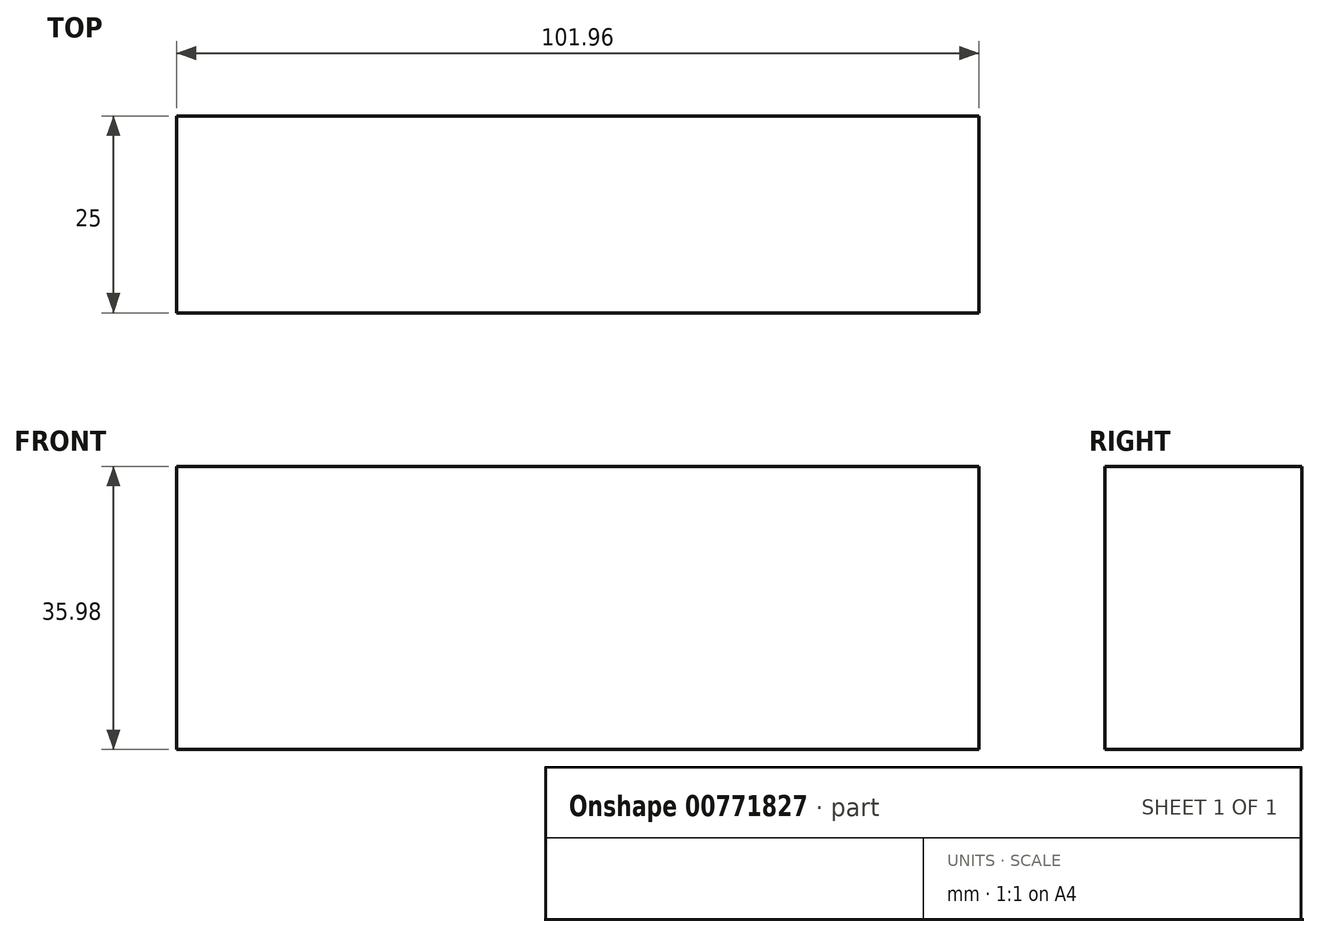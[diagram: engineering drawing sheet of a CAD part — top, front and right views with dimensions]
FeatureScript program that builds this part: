
annotation { "Feature Type Name" : "Feature", "Feature Type Description" : "" }
export const myFeature = defineFeature(function(context is Context, id is Id, definition is map)
    precondition{}
    {
        {
            var Q0;
            Q0=qCreatedBy(makeId("Front.planeOp"),FACE);
            var sketch = newSketch(context, id + "F0", { "sketchPlane" : qUnion([Q0])});
            skLineSegment(sketch, "E0.bottom", {"start": v(-51.27, 49.73) * mm, "end": v(50.69, 49.73) * mm});
            skLineSegment(sketch, "E0.top", {"start": v(-51.27, 13.75) * mm, "end": v(50.69, 13.75) * mm});
            skLineSegment(sketch, "E0.left", {"start": v(-51.27, 49.73) * mm, "end": v(-51.27, 13.75) * mm});
            skLineSegment(sketch, "E0.right", {"start": v(50.69, 49.73) * mm, "end": v(50.69, 13.75) * mm});
            skSolve(sketch);
        }
        {
            var Q0;
            Q0 = qSketchRegion(id + "F0", true);
            extrude(context, id + "F1", {"entities" : qUnion([Q0]), "depth" : 25 * mm, "offsetDistance" : 25 * mm});
        }
    });
